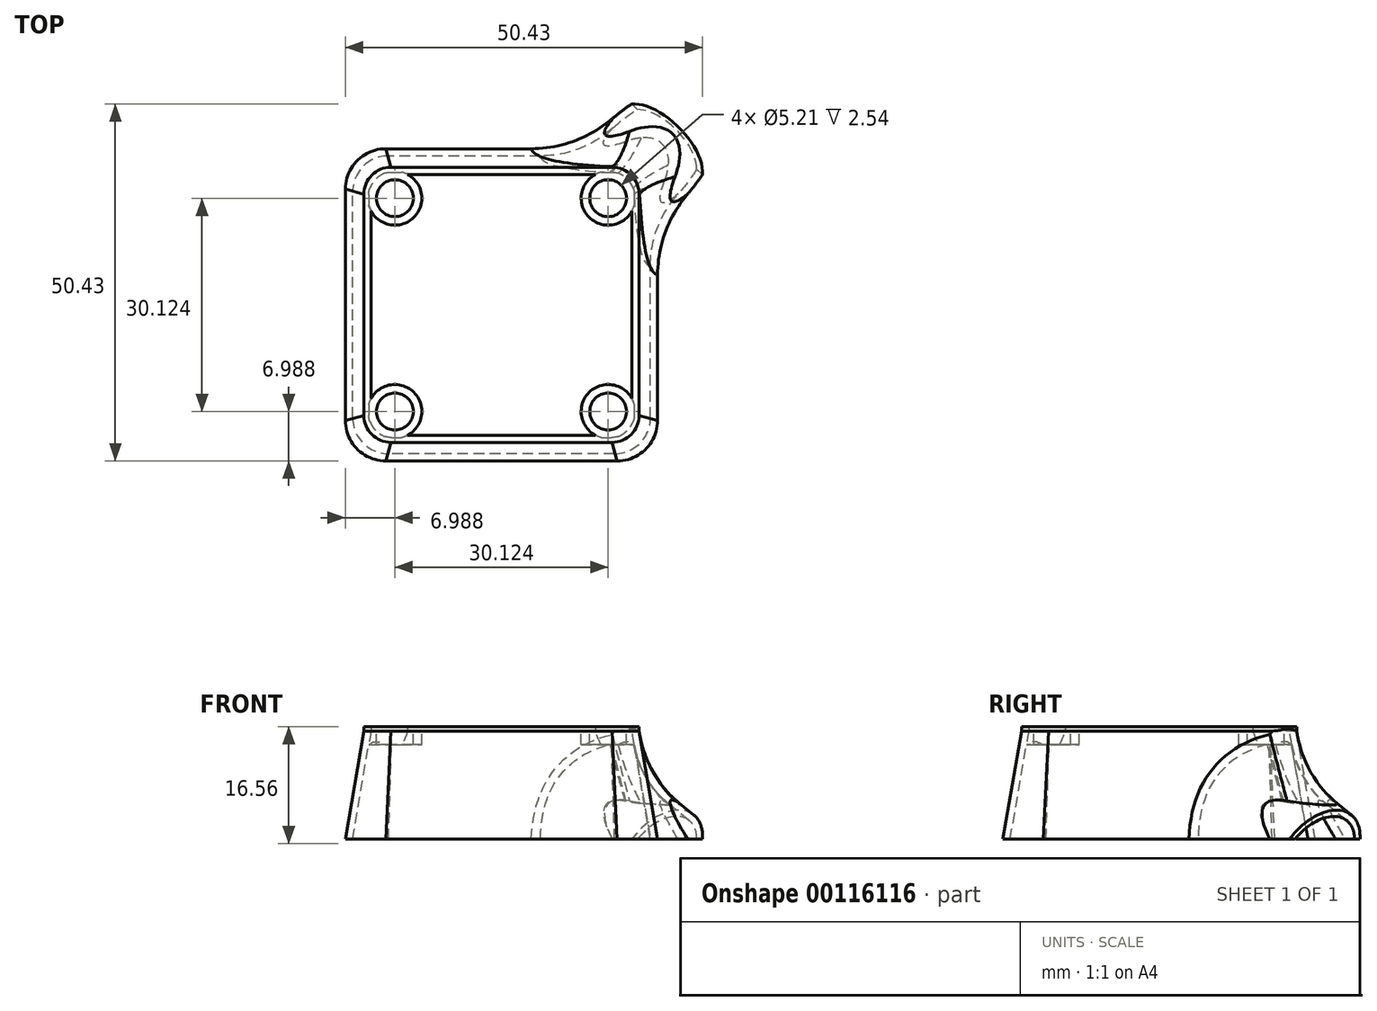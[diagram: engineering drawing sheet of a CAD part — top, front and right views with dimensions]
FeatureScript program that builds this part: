
annotation { "Feature Type Name" : "Feature", "Feature Type Description" : "" }
export const myFeature = defineFeature(function(context is Context, id is Id, definition is map)
    precondition{}
    {
        {
            var Q0;
            Q0=qCreatedBy(makeId("Top.planeOp"),FACE);
            var sketch = newSketch(context, id + "F0", { "sketchPlane" : qUnion([Q0])});
            skLineSegment(sketch, "E0.bottom", {"start": v(15.62, 19.43) * mm, "end": v(-15.62, 19.43) * mm});
            skLineSegment(sketch, "E0.top", {"start": v(15.62, -19.43) * mm, "end": v(-15.62, -19.43) * mm});
            skLineSegment(sketch, "E0.left", {"start": v(19.43, 15.62) * mm, "end": v(19.43, -15.62) * mm});
            skLineSegment(sketch, "E0.right", {"start": v(-19.43, 15.62) * mm, "end": v(-19.43, -15.62) * mm});
            skPoint(sketch, "E0.middle", {"position": v(0, 0) * mm});
            skPoint(sketch, "E1.visualSharp", {"position": v(-19.43, 19.43) * mm});
            skArc(sketch, "E1.filletArc", {"start": v(-15.62, 19.43) * mm, "mid": v(-18.32, 18.32) * mm, "end": v(-19.43, 15.62) * mm});
            skPoint(sketch, "E2.visualSharp", {"position": v(19.43, 19.43) * mm});
            skArc(sketch, "E2.filletArc", {"start": v(19.43, 15.62) * mm, "mid": v(18.32, 18.32) * mm, "end": v(15.62, 19.43) * mm});
            skPoint(sketch, "E3.visualSharp", {"position": v(19.43, -19.43) * mm});
            skArc(sketch, "E3.filletArc", {"start": v(15.62, -19.43) * mm, "mid": v(18.32, -18.32) * mm, "end": v(19.43, -15.62) * mm});
            skPoint(sketch, "E4.visualSharp", {"position": v(-19.43, -19.43) * mm});
            skArc(sketch, "E4.filletArc", {"start": v(-19.43, -15.62) * mm, "mid": v(-18.32, -18.32) * mm, "end": v(-15.62, -19.43) * mm});
            skSolve(sketch);
        }
        {
            var Q0;
            Q0=qCreatedBy(makeId("Top.planeOp"),FACE);
            cPlane(context, id + "F1", {"entities" : qUnion([Q0]), "cplaneType" : CPlaneType.OFFSET, "offset" : 15.37 * mm, "oppositeDirection" : true, "width" : 152.4 * mm, "height" : 152.4 * mm});
        }
        {
            var Q0;
            Q0=qCreatedBy(id+"F1.planeOp",FACE);
            var sketch = newSketch(context, id + "F2", { "sketchPlane" : qUnion([Q0])});
            skLineSegment(sketch, "E5.bottom", {"start": v(16.34, 22.06) * mm, "end": v(-16.34, 22.06) * mm});
            skLineSegment(sketch, "E5.top", {"start": v(16.34, -22.06) * mm, "end": v(-16.34, -22.06) * mm});
            skLineSegment(sketch, "E5.left", {"start": v(22.06, 16.34) * mm, "end": v(22.06, -16.34) * mm});
            skLineSegment(sketch, "E5.right", {"start": v(-22.06, 16.34) * mm, "end": v(-22.06, -16.34) * mm});
            skPoint(sketch, "E5.middle", {"position": v(0, 0) * mm});
            skPoint(sketch, "E6.visualSharp", {"position": v(-22.06, 22.06) * mm});
            skArc(sketch, "E6.filletArc", {"start": v(-16.34, 22.06) * mm, "mid": v(-20.39, 20.39) * mm, "end": v(-22.06, 16.34) * mm});
            skPoint(sketch, "E7.visualSharp", {"position": v(22.06, 22.06) * mm});
            skArc(sketch, "E7.filletArc", {"start": v(22.06, 16.34) * mm, "mid": v(20.39, 20.39) * mm, "end": v(16.34, 22.06) * mm});
            skPoint(sketch, "E8.visualSharp", {"position": v(22.06, -22.06) * mm});
            skArc(sketch, "E8.filletArc", {"start": v(16.34, -22.06) * mm, "mid": v(20.39, -20.39) * mm, "end": v(22.06, -16.34) * mm});
            skPoint(sketch, "E9.visualSharp", {"position": v(-22.06, -22.06) * mm});
            skArc(sketch, "E9.filletArc", {"start": v(-22.06, -16.34) * mm, "mid": v(-20.39, -20.39) * mm, "end": v(-16.34, -22.06) * mm});
            skSolve(sketch);
        }
        {
            var Q0;
            Q0=makeQuery(id+"F2.imprint","IMPRINT",FACE,{"disambiguationData":[TD([[makeQuery(id+"F2.imprint","IMPRINT",EDGE,{"derivedFrom":sQuery(id+"F2.wireOp",EDGE,"E5.bottom")}),1.0]])]});
            var Q1;
            Q1=makeQuery(id+"F0.imprint","IMPRINT",FACE,{"disambiguationData":[TD([[makeQuery(id+"F0.imprint","IMPRINT",EDGE,{"derivedFrom":sQuery(id+"F0.wireOp",EDGE,"E0.bottom")}),1.0]])]});
            loft(context, id + "F3", {"sheetProfilesArray" : [{ "sheetProfileEntities" : qUnion([Q0]) }, { "sheetProfileEntities" : qUnion([Q1]) }]});
        }
        {
            var Q0;
            Q0=makeQuery(id+"F3.opLoft","CAP_FACE",FACE,{"disambiguationData":[OSD([makeQuery(id+"F0.imprint","IMPRINT",FACE,{"disambiguationData":[TD([[makeQuery(id+"F0.imprint","IMPRINT",EDGE,{"derivedFrom":sQuery(id+"F0.wireOp",EDGE,"E0.bottom")}),1.0]])]})])],"isStart":true});
            var sketch = newSketch(context, id + "F4", { "sketchPlane" : qUnion([Q0])});
            skLineSegment(sketch, "E10.bottom", {"start": v(15.5, 18.42) * mm, "end": v(-15.5, 18.42) * mm});
            skLineSegment(sketch, "E10.top", {"start": v(15.5, -18.42) * mm, "end": v(-15.5, -18.42) * mm});
            skLineSegment(sketch, "E10.left", {"start": v(18.42, 15.5) * mm, "end": v(18.42, -15.5) * mm});
            skLineSegment(sketch, "E10.right", {"start": v(-18.42, 15.5) * mm, "end": v(-18.42, -15.5) * mm});
            skPoint(sketch, "E10.middle", {"position": v(0, 0) * mm});
            skPoint(sketch, "E11.visualSharp", {"position": v(18.42, 18.42) * mm});
            skArc(sketch, "E11.filletArc", {"start": v(18.42, 15.5) * mm, "mid": v(17.56, 17.56) * mm, "end": v(15.5, 18.42) * mm});
            skPoint(sketch, "E12.visualSharp", {"position": v(-18.42, 18.42) * mm});
            skArc(sketch, "E12.filletArc", {"start": v(-15.5, 18.42) * mm, "mid": v(-17.56, 17.56) * mm, "end": v(-18.42, 15.5) * mm});
            skPoint(sketch, "E13.visualSharp", {"position": v(-18.42, -18.42) * mm});
            skArc(sketch, "E13.filletArc", {"start": v(-18.42, -15.5) * mm, "mid": v(-17.56, -17.56) * mm, "end": v(-15.5, -18.42) * mm});
            skPoint(sketch, "E14.visualSharp", {"position": v(18.42, -18.42) * mm});
            skArc(sketch, "E14.filletArc", {"start": v(15.5, -18.41) * mm, "mid": v(17.56, -17.56) * mm, "end": v(18.41, -15.5) * mm});
            skSolve(sketch);
        }
        {
            var Q0;
            Q0=makeQuery(id+"F3.opLoft","CAP_FACE",FACE,{"disambiguationData":[OSD([makeQuery(id+"F2.imprint","IMPRINT",FACE,{"disambiguationData":[TD([[makeQuery(id+"F2.imprint","IMPRINT",EDGE,{"derivedFrom":sQuery(id+"F2.wireOp",EDGE,"E5.bottom")}),1.0]])]})])],"isStart":true});
            var sketch = newSketch(context, id + "F5", { "sketchPlane" : qUnion([Q0])});
            skLineSegment(sketch, "E15.bottom", {"start": v(15.96, 21.04) * mm, "end": v(-15.96, 21.04) * mm});
            skLineSegment(sketch, "E15.top", {"start": v(15.96, -21.04) * mm, "end": v(-15.96, -21.04) * mm});
            skLineSegment(sketch, "E15.left", {"start": v(21.04, 15.96) * mm, "end": v(21.04, -15.96) * mm});
            skLineSegment(sketch, "E15.right", {"start": v(-21.04, 15.96) * mm, "end": v(-21.04, -15.96) * mm});
            skPoint(sketch, "E15.middle", {"position": v(0, 0) * mm});
            skPoint(sketch, "E16.visualSharp", {"position": v(-21.04, 21.04) * mm});
            skArc(sketch, "E16.filletArc", {"start": v(-15.96, 21.04) * mm, "mid": v(-19.56, 19.56) * mm, "end": v(-21.04, 15.96) * mm});
            skPoint(sketch, "E17.visualSharp", {"position": v(21.04, 21.04) * mm});
            skArc(sketch, "E17.filletArc", {"start": v(21.04, 15.96) * mm, "mid": v(19.56, 19.56) * mm, "end": v(15.96, 21.04) * mm});
            skPoint(sketch, "E18.visualSharp", {"position": v(21.04, -21.04) * mm});
            skArc(sketch, "E18.filletArc", {"start": v(15.96, -21.04) * mm, "mid": v(19.56, -19.56) * mm, "end": v(21.04, -15.96) * mm});
            skPoint(sketch, "E19.visualSharp", {"position": v(-21.04, -21.04) * mm});
            skArc(sketch, "E19.filletArc", {"start": v(-21.04, -15.96) * mm, "mid": v(-19.56, -19.56) * mm, "end": v(-15.96, -21.04) * mm});
            skSolve(sketch);
        }
        {
            var Q1;
            Q1=makeQuery(id+"F5.imprint","IMPRINT",FACE,{"disambiguationData":[TD([[makeQuery(id+"F5.imprint","IMPRINT",EDGE,{"derivedFrom":sQuery(id+"F5.wireOp",EDGE,"E15.bottom")}),1.0]])]});
            var Q2;
            Q2=makeQuery(id+"F4.imprint","IMPRINT",FACE,{"disambiguationData":[TD([[makeQuery(id+"F4.imprint","IMPRINT",EDGE,{"derivedFrom":sQuery(id+"F4.wireOp",EDGE,"E10.bottom")}),1.0]])]});
            loft(context, id + "F6", {"operationType" : NewBodyOperationType.REMOVE, "sheetProfilesArray" : [{ "sheetProfileEntities" : qUnion([Q1]) }, { "sheetProfileEntities" : qUnion([Q2]) }]});
        }
        {
            var Q0;
            Q0=makeQuery(id+"F3.opLoft","CAP_FACE",FACE,{"disambiguationData":[OSD([makeQuery(id+"F0.imprint","IMPRINT",FACE,{"disambiguationData":[TD([[makeQuery(id+"F0.imprint","IMPRINT",EDGE,{"derivedFrom":sQuery(id+"F0.wireOp",EDGE,"E0.bottom")}),1.0]])]})])],"isStart":true});
            var sketch = newSketch(context, id + "F7", { "sketchPlane" : qUnion([Q0])});
            skCircle(sketch, "E20", {"center": v(-15.06, 15.06) * mm, "radius": 2.6 * mm});
            skCircle(sketch, "E21", {"center": v(15.06, 15.06) * mm, "radius": 2.6 * mm});
            skCircle(sketch, "E22", {"center": v(15.06, -15.06) * mm, "radius": 2.6 * mm});
            skCircle(sketch, "E23", {"center": v(-15.06, -15.06) * mm, "radius": 2.6 * mm});
            skCircle(sketch, "E24", {"center": v(-15.06, 15.06) * mm, "radius": 3.81 * mm});
            skCircle(sketch, "E25", {"center": v(15.06, 15.06) * mm, "radius": 3.81 * mm});
            skCircle(sketch, "E26", {"center": v(15.06, -15.06) * mm, "radius": 3.81 * mm});
            skCircle(sketch, "E27", {"center": v(-15.06, -15.06) * mm, "radius": 3.81 * mm});
            skSolve(sketch);
        }
        {
            var Q0;
            Q0 = qSketchRegion(id + "F7", true);
            extrude(context, id + "F8", {"entities" : qUnion([Q0]), "operationType" : NewBodyOperationType.ADD, "oppositeDirection" : true, "depth" : 1.9 * mm});
        }
        {
            var Q0;
            Q0=makeQuery(id+"F8.boolean.opBoolean","MERGE",FACE,{"derivedFrom":[makeQuery(id+"F3.opLoft","CAP_FACE",FACE,{"disambiguationData":[OSD([makeQuery(id+"F0.imprint","IMPRINT",FACE,{"disambiguationData":[TD([[makeQuery(id+"F0.imprint","IMPRINT",EDGE,{"derivedFrom":sQuery(id+"F0.wireOp",EDGE,"E0.bottom")}),1.0]])]})])],"isStart":true}),makeQuery(id+"F8.opExtrude","CAP_FACE",FACE,{"disambiguationData":[OSD([sQuery(id+"F7.wireOp",EDGE,"E20"),sQuery(id+"F7.wireOp",EDGE,"E24")])],"isStart":true}),makeQuery(id+"F8.opExtrude","CAP_FACE",FACE,{"disambiguationData":[OSD([sQuery(id+"F7.wireOp",EDGE,"E21"),sQuery(id+"F7.wireOp",EDGE,"E25")])],"isStart":true}),makeQuery(id+"F8.opExtrude","CAP_FACE",FACE,{"disambiguationData":[OSD([sQuery(id+"F7.wireOp",EDGE,"E22"),sQuery(id+"F7.wireOp",EDGE,"E26")])],"isStart":true}),makeQuery(id+"F8.opExtrude","CAP_FACE",FACE,{"disambiguationData":[OSD([sQuery(id+"F7.wireOp",EDGE,"E23"),sQuery(id+"F7.wireOp",EDGE,"E27")])],"isStart":true})]});
            extrude(context, id + "F9", {"entities" : qUnion([Q0]), "operationType" : NewBodyOperationType.ADD, "depth" : 0.64 * mm});
        }
        {
            var Q0;
            Q0=qCreatedBy(id+"F1.planeOp",FACE);
            var sketch = newSketch(context, id + "F10", { "sketchPlane" : qUnion([Q0])});
            skLineSegment(sketch, "E28", {"start": v(-26.94, -26.94) * mm, "end": v(26.94, 26.94) * mm});
            skLineSegment(sketch, "E29", {"start": v(-26.94, 26.94) * mm, "end": v(26.94, -26.94) * mm});
            skSolve(sketch);
        }
        {
            var Q0;
            Q0=qCreatedBy(makeId("Front.planeOp"),FACE);
            var Q1;
            Q1=sQuery(id+"F10.wireOp",EDGE,"E28");
            cPlane(context, id + "F11", {"entities" : qUnion([Q0, Q1]), "cplaneType" : CPlaneType.LINE_ANGLE, "offset" : 25.4 * mm, "angle" : 0 * degree, "width" : 152.4 * mm, "height" : 152.4 * mm});
        }
        {
            var Q0;
            Q0=qCreatedBy(makeId("Front.planeOp"),FACE);
            var Q1;
            Q1=sQuery(id+"F10.wireOp",EDGE,"E29");
            cPlane(context, id + "F12", {"entities" : qUnion([Q0, Q1]), "cplaneType" : CPlaneType.LINE_ANGLE, "offset" : 25.4 * mm, "angle" : 0 * degree, "width" : 152.4 * mm, "height" : 152.4 * mm});
        }
        {
            var Q0;
            Q0=qCreatedBy(id+"F11.planeOp",FACE);
            var sketch = newSketch(context, id + "F13", { "sketchPlane" : qUnion([Q0])});
            skLineSegment(sketch, "E30", {"start": v(33.02, -15.37) * mm, "end": v(36.26, -9.76) * mm});
            skLineSegment(sketch, "E31", {"start": v(-33.02, -15.37) * mm, "end": v(-36.26, -9.76) * mm});
            skSolve(sketch);
        }
        {
            var Q0;
            Q0=qCreatedBy(id+"F12.planeOp",FACE);
            var Q1;
            Q1=sQuery(id+"F13.wireOp",EDGE,"E31");
            cPlane(context, id + "F14", {"entities" : qUnion([Q0, Q1]), "cplaneType" : CPlaneType.LINE_ANGLE, "offset" : 25.4 * mm, "angle" : 0 * degree, "width" : 152.4 * mm, "height" : 152.4 * mm});
        }
        {
            var Q0;
            Q0=qCreatedBy(id+"F14.planeOp",FACE);
            var sketch = newSketch(context, id + "F15", { "sketchPlane" : qUnion([Q0])});
            skCircle(sketch, "E32", {"center": v(0.18, 0.36) * mm, "radius": 7.62 * mm});
            skCircle(sketch, "E33", {"center": v(0.18, 0.36) * mm, "radius": 6.6 * mm});
            skLineSegment(sketch, "E34", {"start": v(-3.92, 5.54) * mm, "end": v(-4.9, 6.03) * mm});
            skLineSegment(sketch, "E35", {"start": v(6.78, 0.19) * mm, "end": v(7.77, -0.3) * mm});
            skSolve(sketch);
        }
        {
            var Q0;
            Q0=makeQuery(id+"F3.opLoft","CAP_FACE",FACE,{"disambiguationData":[OSD([makeQuery(id+"F2.imprint","IMPRINT",FACE,{"disambiguationData":[TD([[makeQuery(id+"F2.imprint","IMPRINT",EDGE,{"derivedFrom":sQuery(id+"F2.wireOp",EDGE,"E5.bottom")}),1.0]])]})])],"isStart":true});
            extrude(context, id + "F16", {"entities" : qUnion([Q0]), "operationType" : NewBodyOperationType.ADD, "depth" : 25.4 * mm});
        }
        {
            var Q0;
            {var subQ0=sQuery(id+"F15.wireOp",EDGE,"E34");Q0=makeQuery(id+"F15.imprint","IMPRINT",FACE,{"disambiguationData":[TD([[makeQuery(id+"F15.imprint","IMPRINT",EDGE,{"derivedFrom":subQ0}),-1.0]])]});}
            var Q1;
            Q1=makeQuery(id+"F3.opLoft","SWEPT_FACE",FACE,{"disambiguationData":[OSD([sQuery(id+"F0.wireOp",EDGE,"E0.left"),sQuery(id+"F0.wireOp",EDGE,"E2.filletArc"),sQuery(id+"F0.wireOp",EDGE,"E3.filletArc"),sQuery(id+"F2.wireOp",EDGE,"E5.left"),sQuery(id+"F2.wireOp",EDGE,"E7.filletArc"),sQuery(id+"F2.wireOp",EDGE,"E8.filletArc")])]});
            var Q2;
            {var subQ0=sQuery(id+"F15.wireOp",EDGE,"E34");Q2=makeQuery(id+"F15.imprint","IMPRINT",FACE,{"disambiguationData":[TD([[makeQuery(id+"F15.imprint","IMPRINT",EDGE,{"derivedFrom":subQ0}),1.0]])]});}
            var Q3;
            Q3=makeQuery(id+"F3.opLoft","SWEPT_FACE",FACE,{"disambiguationData":[OSD([sQuery(id+"F0.wireOp",EDGE,"E0.bottom"),sQuery(id+"F0.wireOp",EDGE,"E0.left"),sQuery(id+"F0.wireOp",EDGE,"E2.filletArc"),sQuery(id+"F2.wireOp",EDGE,"E5.bottom"),sQuery(id+"F2.wireOp",EDGE,"E5.left"),sQuery(id+"F2.wireOp",EDGE,"E7.filletArc")])]});
            var Q4;
            Q4=makeQuery(id+"F3.opLoft","SWEPT_BODY",BODY,{"disambiguationData":[OSD([makeQuery(id+"F0.imprint","IMPRINT",FACE,{"disambiguationData":[TD([[makeQuery(id+"F0.imprint","IMPRINT",EDGE,{"derivedFrom":sQuery(id+"F0.wireOp",EDGE,"E0.bottom")}),1.0]])]}),makeQuery(id+"F2.imprint","IMPRINT",FACE,{"disambiguationData":[TD([[makeQuery(id+"F2.imprint","IMPRINT",EDGE,{"derivedFrom":sQuery(id+"F2.wireOp",EDGE,"E5.bottom")}),1.0]])]})])]});
            extrude(context, id + "F17", {"entities" : qUnion([Q0, Q1, Q2]), "operationType" : NewBodyOperationType.ADD, "endBound" : BoundingType.UP_TO_BODY, "endBoundEntityFace" : qUnion([Q3]), "endBoundEntityBody" : qUnion([Q4]), "depth" : 25.4 * mm});
        }
        {
            var Q0;
            Q0=qCreatedBy(makeId("Right.planeOp"),FACE);
            var sketch = newSketch(context, id + "F18", { "sketchPlane" : qUnion([Q0])});
            skLineSegment(sketch, "E36.bottom", {"start": v(-43.88, -15.3) * mm, "end": v(43.88, -15.3) * mm});
            skLineSegment(sketch, "E36.top", {"start": v(-43.88, -44.62) * mm, "end": v(43.88, -44.62) * mm});
            skLineSegment(sketch, "E36.left", {"start": v(-43.88, -15.3) * mm, "end": v(-43.88, -44.62) * mm});
            skLineSegment(sketch, "E36.right", {"start": v(43.88, -15.3) * mm, "end": v(43.88, -44.62) * mm});
            skPoint(sketch, "E36.middle", {"position": v(0, -29.95) * mm});
            skSolve(sketch);
        }
        {
            var Q0;
            Q0 = qSketchRegion(id + "F18", true);
            extrude(context, id + "F19", {"entities" : qUnion([Q0]), "operationType" : NewBodyOperationType.REMOVE, "endBound" : BoundingType.SYMMETRIC, "oppositeDirection" : true, "depth" : 76.2 * mm});
        }
        {
            var Q0;
            Q0=makeQuery(id+"F17.boolean.opBoolean","INTERSECT",EDGE,{"derivedFrom":[makeQuery(id+"F3.opLoft","SWEPT_FACE",FACE,{"disambiguationData":[OSD([sQuery(id+"F0.wireOp",EDGE,"E0.bottom"),sQuery(id+"F0.wireOp",EDGE,"E1.filletArc"),sQuery(id+"F0.wireOp",EDGE,"E2.filletArc"),sQuery(id+"F2.wireOp",EDGE,"E5.bottom"),sQuery(id+"F2.wireOp",EDGE,"E6.filletArc"),sQuery(id+"F2.wireOp",EDGE,"E7.filletArc")])]}),makeQuery(id+"F17.opExtrude","SWEPT_FACE",FACE,{"disambiguationData":[OSD([sQuery(id+"F15.wireOp",EDGE,"E32")])]})]});
            fillet(context, id + "F20", {"entities" : qUnion([Q0]), "radius" : 17.78 * mm, "tangentPropagation" : true, "allowEdgeOverflow" : false});
        }
        {
            var Q0;
            {var subQ0=sQuery(id+"F15.wireOp",EDGE,"E33");var subQ1=makeQuery(id+"F15.imprint","INTERSECT",VERTEX,{"derivedFrom":[subQ0,sQuery(id+"F15.wireOp",EDGE,"E34")]});Q0=makeQuery(id+"F15.imprint","IMPRINT",FACE,{"disambiguationData":[TD([[makeQuery(id+"F15.imprint","IMPRINT",EDGE,{"disambiguationData":[TD([[subQ1,1.0]])],"derivedFrom":subQ0}),1.0]])]});}
            extrude(context, id + "F21", {"entities" : qUnion([Q0]), "operationType" : NewBodyOperationType.REMOVE, "depth" : 25.4 * mm});
        }
        {
            var Q0;
            Q0=makeQuery(id+"F21.boolean.opBoolean","INTERSECT",EDGE,{"derivedFrom":[makeQuery(id+"F6.boolean.opBoolean","COPY",FACE,{"derivedFrom":makeQuery(id+"F6.opLoft","SWEPT_FACE",FACE,{"disambiguationData":[OSD([sQuery(id+"F4.wireOp",EDGE,"E10.bottom"),sQuery(id+"F4.wireOp",EDGE,"E10.left"),sQuery(id+"F4.wireOp",EDGE,"E11.filletArc"),sQuery(id+"F5.wireOp",EDGE,"E15.top"),sQuery(id+"F5.wireOp",EDGE,"E15.left"),sQuery(id+"F5.wireOp",EDGE,"E18.filletArc")])]})}),makeQuery(id+"F21.opExtrude","SWEPT_FACE",FACE,{"disambiguationData":[OSD([sQuery(id+"F15.wireOp",EDGE,"E33")])]})]});
            fillet(context, id + "F22", {"entities" : qUnion([Q0]), "radius" : 15.24 * mm, "tangentPropagation" : true, "allowEdgeOverflow" : false});
        }
    });
